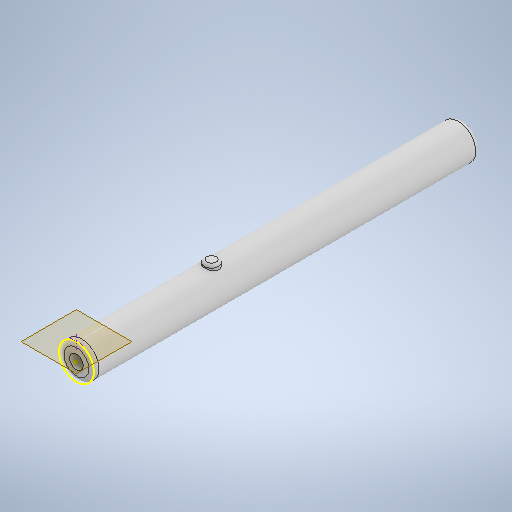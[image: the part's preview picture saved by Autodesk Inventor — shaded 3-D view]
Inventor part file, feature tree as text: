
AUTODESK INVENTOR PART (.ipt)
format: ipt  version: 2025 (Build 290162000, 162)  size: 278,528 bytes
history: native  units: mm
features: sketch x4, extrude x3, fillet x2, plane x1
ambient origin geometry x8: Origin, YZ Plane, XZ Plane, XY Plane, X Axis, Y Axis, Z Axis, Center Point
bodies: Solid1 (feature_tree)
feature tree (10):
  extrude  "Extrusion1"  Depth=153.5mm TaperAngle=0.0deg
  sketch  "Sketch2"  dims[d3=50.71mm d4=5.75mm d5=2.92mm d6=0.0mm]
  plane  "Work Plane1"
  extrude  "Extrusion2"  Depth=5.75mm
  fillet  "Fillet1"  Radius=2.92mm
  extrude  "Extrusion3"  Depth=5.5mm
  fillet  "Fillet2"  Radius=30.0mm
  sketch  "Sketch1"  dims[d0=13.85mm d1=153.5mm d2=0.0mm]
  sketch  "Sketch3"  dims[d7=1.0mm d8=5.5mm d9=30.0mm d10=0.0mm]
  sketch  "Sketch4"  dims[d11=2.0mm]
